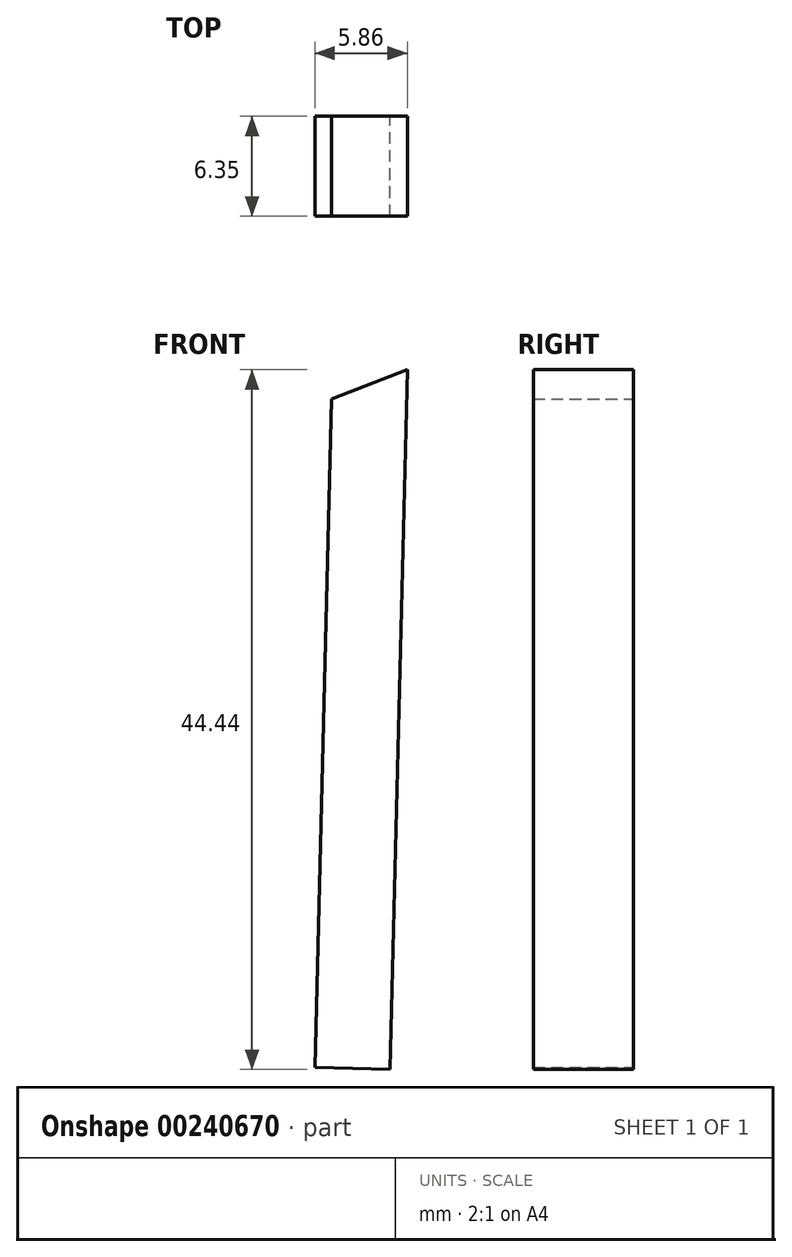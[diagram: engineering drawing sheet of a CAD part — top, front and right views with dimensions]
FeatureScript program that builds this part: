
annotation { "Feature Type Name" : "Feature", "Feature Type Description" : "" }
export const myFeature = defineFeature(function(context is Context, id is Id, definition is map)
    precondition{}
    {
        {
            var Q0;
            Q0=qCreatedBy(makeId("Front.planeOp"),FACE);
            var sketch = newSketch(context, id + "F0", { "sketchPlane" : qUnion([Q0])});
            skLineSegment(sketch, "E0.bottom", {"start": v(1.83, -22.28) * mm, "end": v(-2.93, -22.16) * mm});
            skLineSegment(sketch, "E0.left", {"start": v(1.83, -22.28) * mm, "end": v(2.93, 22.16) * mm});
            skLineSegment(sketch, "E0.right", {"start": v(-2.93, -22.16) * mm, "end": v(-1.88, 20.3) * mm});
            skPoint(sketch, "E0.middle", {"position": v(0, 0) * mm});
            skLineSegment(sketch, "E1", {"start": v(2.93, 22.16) * mm, "end": v(-1.88, 20.3) * mm});
            skPoint(sketch, "E2.orphan", {"position": v(-1.83, 22.28) * mm});
            skSolve(sketch);
        }
        {
            var Q0;
            Q0 = qSketchRegion(id + "F0", true);
            extrude(context, id + "F1", {"entities" : qUnion([Q0]), "depth" : 6.35 * mm});
        }
    });
